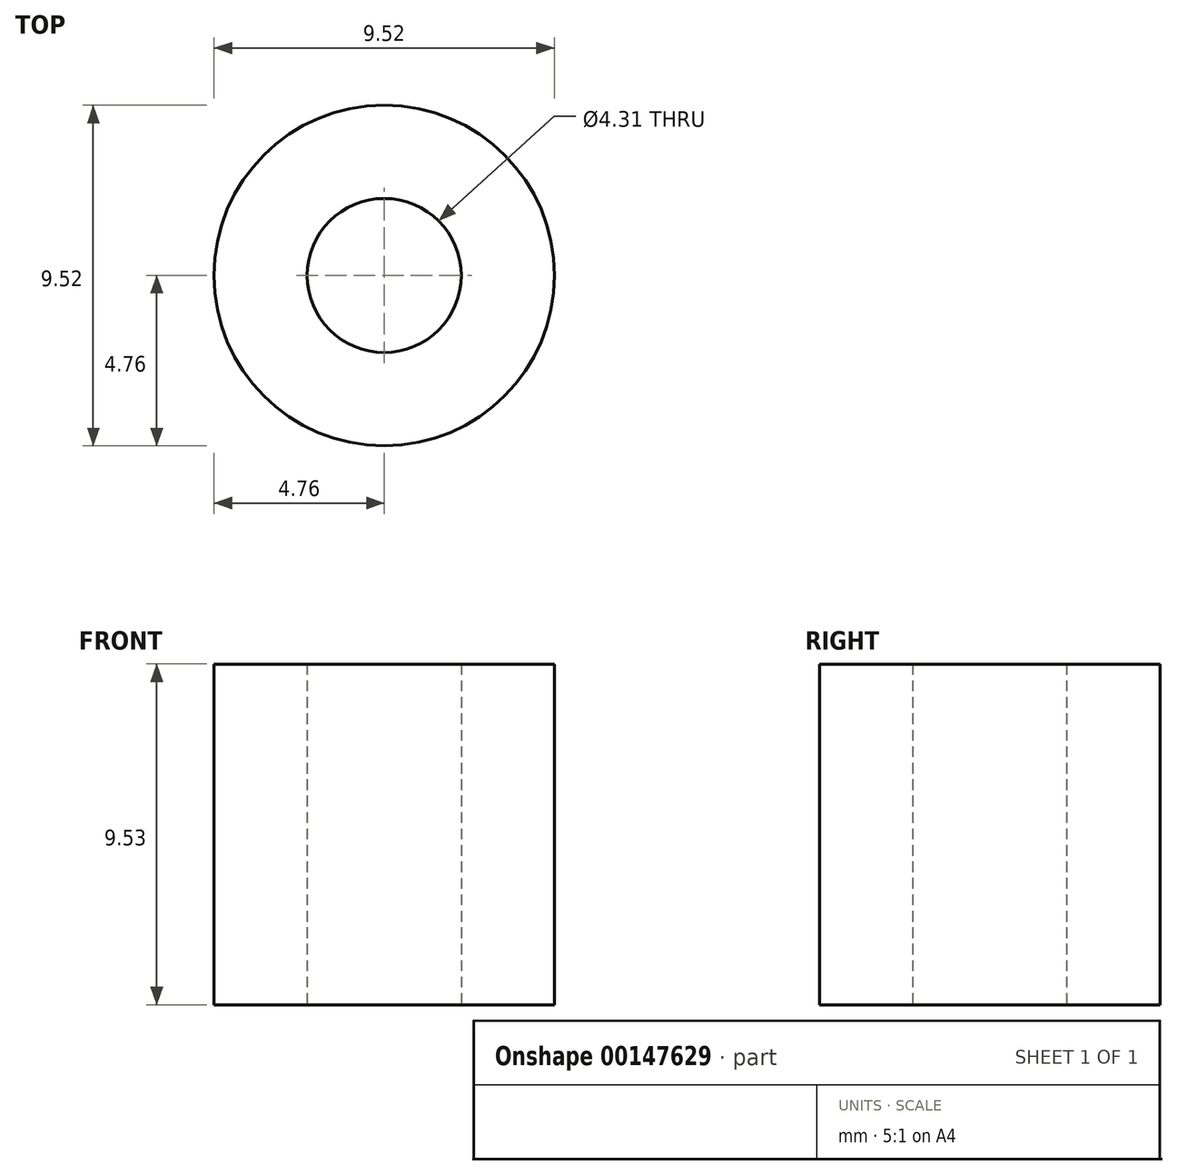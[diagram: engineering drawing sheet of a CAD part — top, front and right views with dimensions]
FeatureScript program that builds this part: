
annotation { "Feature Type Name" : "Feature", "Feature Type Description" : "" }
export const myFeature = defineFeature(function(context is Context, id is Id, definition is map)
    precondition{}
    {
        {
            var Q0;
            Q0=qCreatedBy(makeId("Top.planeOp"),FACE);
            var sketch = newSketch(context, id + "F0", { "sketchPlane" : qUnion([Q0])});
            skCircle(sketch, "E0", {"center": v(0, 0) * mm, "radius": 4.76 * mm});
            skCircle(sketch, "E1", {"center": v(0, 0) * mm, "radius": 2.15 * mm});
            skSolve(sketch);
        }
        {
            var Q0;
            Q0=qSketchRegion(id+"F0",true);
            extrude(context, id + "F1", {"entities" : qUnion([Q0]), "depth" : 9.52 * mm});
        }
    });
